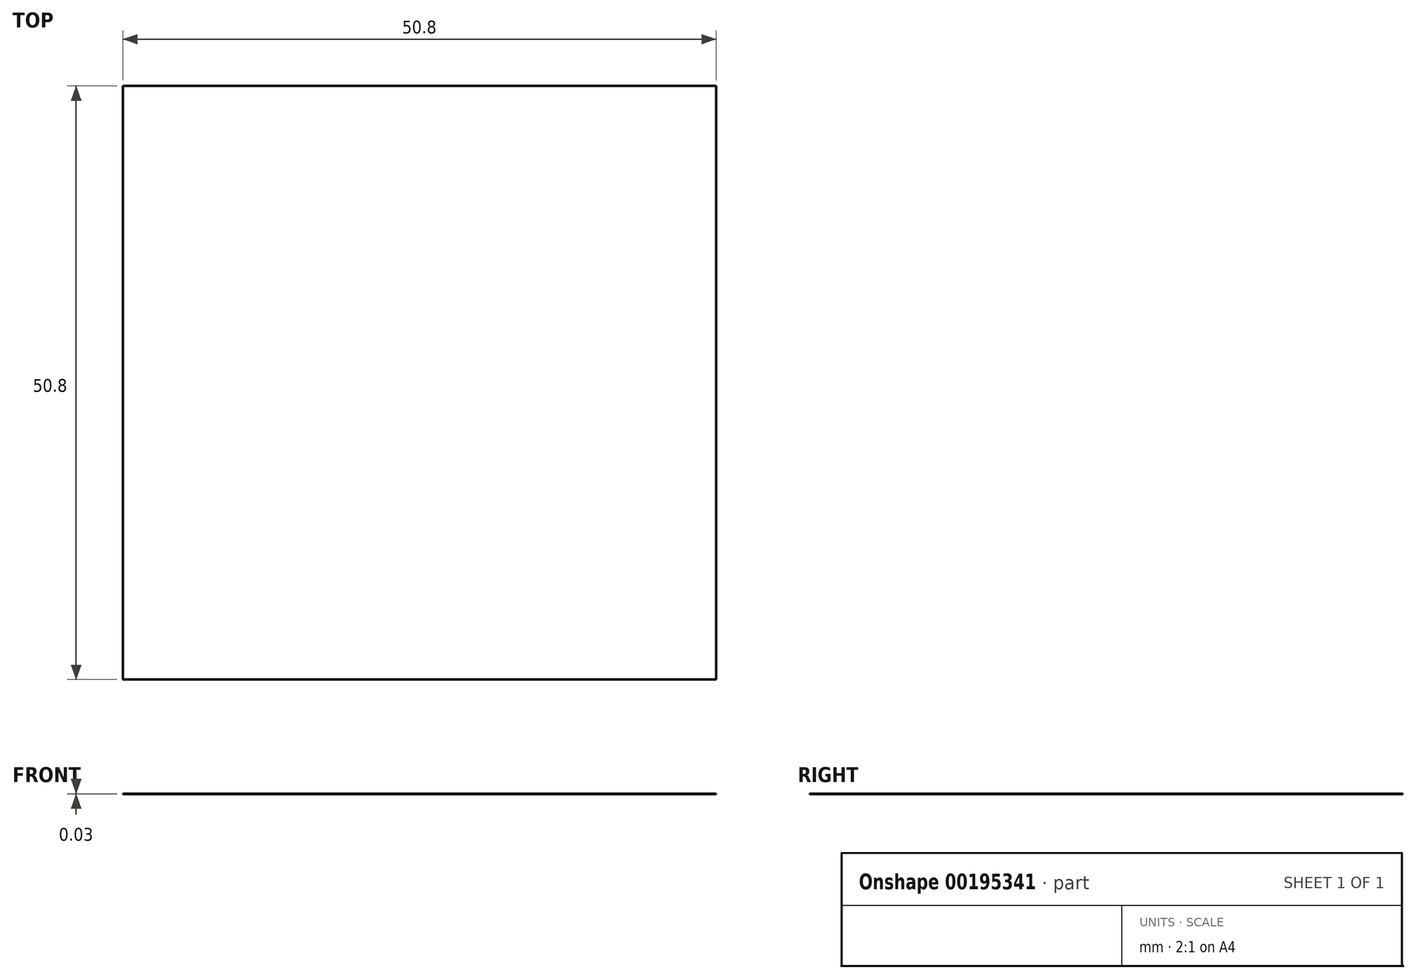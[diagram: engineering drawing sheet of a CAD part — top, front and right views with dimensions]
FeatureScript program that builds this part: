
annotation { "Feature Type Name" : "Feature", "Feature Type Description" : "" }
export const myFeature = defineFeature(function(context is Context, id is Id, definition is map)
    precondition{}
    {
        {
            var Q0;
            Q0=qCreatedBy(makeId("Top.planeOp"),FACE);
            var sketch = newSketch(context, id + "F0", { "sketchPlane" : qUnion([Q0])});
            skLineSegment(sketch, "E0.bottom", {"start": v(25.4, 25.4) * mm, "end": v(-25.4, 25.4) * mm});
            skLineSegment(sketch, "E0.top", {"start": v(25.4, -25.4) * mm, "end": v(-25.4, -25.4) * mm});
            skLineSegment(sketch, "E0.left", {"start": v(25.4, 25.4) * mm, "end": v(25.4, -25.4) * mm});
            skLineSegment(sketch, "E0.right", {"start": v(-25.4, 25.4) * mm, "end": v(-25.4, -25.4) * mm});
            skPoint(sketch, "E0.middle", {"position": v(0, 0) * mm});
            skSolve(sketch);
        }
        {
            var Q0;
            Q0 = qSketchRegion(id + "F0", true);
            extrude(context, id + "F1", {"entities" : qUnion([Q0]), "depth" : 0.03 * mm});
        }
    });
